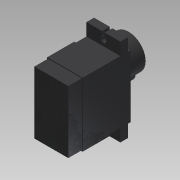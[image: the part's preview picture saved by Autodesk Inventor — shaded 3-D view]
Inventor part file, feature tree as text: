
AUTODESK INVENTOR PART (.ipt)
format: ipt  version: 2016 (Build 200138000, 138)  size: 254,464 bytes
history: native  units: mm
features: extrude x13, sketch x13, projected_geometry x5
ambient origin geometry x8: Origin, YZ Plane, XZ Plane, XY Plane, X Axis, Y Axis, Z Axis, Center Point
bodies: Solid1 (feature_tree)
feature tree (31):
  extrude  "Extrusion1"  Depth=23.0mm
  extrude  "Extrusion2"  Depth=32.2mm
  extrude  "Extrusion3"  Depth=1.0mm TaperAngle=0.0deg
  extrude  "Extrusion4"  Depth=5.5mm TaperAngle=0.0deg
  extrude  "Extrusion5"  Depth=2.8mm TaperAngle=0.0deg
  extrude  "Extrusion6"  Depth=2.0mm TaperAngle=0.0deg
  extrude  "Extrusion7"  Depth=2.0mm TaperAngle=0.0deg
  extrude  "Extrusion8"  Depth=5.0mm
  extrude  "Extrusion9"  Depth=5.0mm
  extrude  "Extrusion11"  Depth=0.3mm TaperAngle=0.0deg
  extrude  "Extrusion12"  Depth=0.3mm TaperAngle=0.0deg
  extrude  "Extrusion13"  Depth=0.3mm TaperAngle=0.0deg
  extrude  "Extrusion14"  [1 undecoded]
  sketch  "Sketch1"  dims[d0=12.5mm d1=23.0mm]
  sketch  "Sketch2"  dims[d2=23.0mm d3=0.0mm d4=32.2mm]
  sketch  "Sketch3"  dims[d5=3.8mm d6=0.0mm d7=1.0mm d8=0.0mm]
  sketch  "Sketch4"  dims[d9=6.25mm d10=5.5mm d11=0.0mm]
  sketch  "Sketch5"  dims[d14=2.8mm d15=7.5mm d16=0.0mm]
  sketch  "Sketch6"  dims[d17=6.95mm d18=2.0mm d19=0.0mm]
  sketch  "Sketch7"  dims[d20=7.0mm d21=2.0mm d22=0.0mm]
  sketch  "Sketch8"  dims[d27=10.0mm d28=0.0mm d29=5.0mm]
  projected_geometry  "Projected Loop1"
  projected_geometry  "Projected Loop2"
  sketch  "Sketch9"  dims[d30=10.0mm d31=0.0mm d32=5.0mm]
  projected_geometry  "Projected Loop3"
  sketch  "Sketch10"  dims[d33=10.0mm d36=0.3mm d37=0.0mm]
  projected_geometry  "Projected Loop4"
  sketch  "Sketch11"  dims[d38=0.3mm d39=0.3mm d40=0.0mm]
  sketch  "Sketch12"  dims[d41=0.3mm d42=0.3mm d43=0.0mm]
  projected_geometry  "Projected Loop5"
  sketch  "Sketch13"  dims[d44=0.3mm d45=0.0mm]
note: 1 required parameter value undecoded (feature->parameter linkage not recoverable at this tier; creation-order binding heuristic only, values carry confidence <= 0.55)
